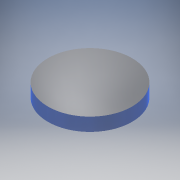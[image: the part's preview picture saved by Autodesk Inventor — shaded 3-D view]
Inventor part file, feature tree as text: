
AUTODESK INVENTOR PART (.ipt)
format: ipt  version: 2016 (Build 200138000, 138)  size: 96,256 bytes
history: native  units: mm
features: extrude x1, sketch x1
ambient origin geometry x8: Origin, YZ Plane, XZ Plane, XY Plane, X Axis, Y Axis, Z Axis, Center Point
bodies: Solid1 (feature_tree)
feature tree (2):
  extrude  "Extrusion1"  Depth=8.0mm TaperAngle=0.0deg
  sketch  "Sketch1"  dims[d0=50.8mm d1=8.0mm d2=0.0mm]
